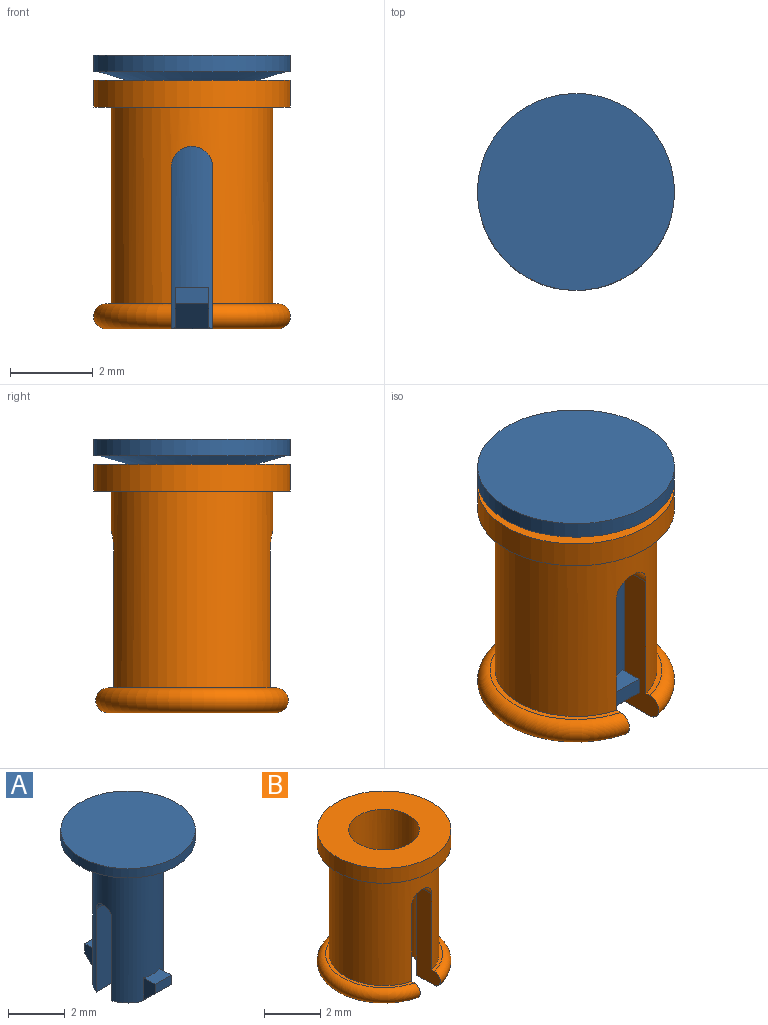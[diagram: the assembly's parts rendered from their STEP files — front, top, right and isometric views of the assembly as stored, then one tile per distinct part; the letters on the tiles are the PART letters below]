
ASSEMBLY  parts=2 mates=1
PART A: 21 faces, bbox 4.8x4.8x6.6 mm
  f0: plane 2.39x0.78mm, normal (0,0,-1), area 1.5mm2, adj f1,f16,f17
  f1: cylinder r=1.25mm len=5.9mm, axis (0,0,1), area 38.8mm2, adj f0,f2,f6,f8,f9,f10,f11,f12
  f2: plane 2.39x0.78mm, normal (0,0,-1), area 1.5mm2, adj f1,f15,f18
  f3: cylinder r=2.38mm len=4.75mm, axis (0,0,1), area 6mm2, adj f4,f5
  f4: plane 4.75x4.75mm, normal (0,0,-1), area 1.8mm2, adj f3,f6
  f5: plane 4.75x4.75mm, normal (0,0,1), area 17.7mm2, adj f3
  f6: cone r=2.25mm half-angle=73.3deg, axis (0,0,1), area 11.5mm2, adj f1,f4
  f7: plane 0.8x0.4mm, normal (0,1,0), area 0.3mm2, adj f8,f9,f10,f16
  f8: plane 0.8x0.57mm, normal (0,0,1), area 0.4mm2, adj f1,f7,f9,f10
  f9: plane 0.97x0.57mm, normal (-1,0,0), area 0.4mm2, adj f1,f7,f8,f16
  f10: plane 0.97x0.57mm, normal (1,0,0), area 0.4mm2, adj f1,f7,f8,f16
  f11: plane 0.8x0.57mm, normal (0,0,1), area 0.4mm2, adj f1,f12,f13,f14
  f12: plane 0.97x0.57mm, normal (1,0,0), area 0.4mm2, adj f1,f11,f14,f15
  f13: plane 0.97x0.57mm, normal (-1,0,0), area 0.4mm2, adj f1,f11,f14,f15
  f14: plane 0.8x0.4mm, normal (0,-1,0), area 0.3mm2, adj f11,f12,f13,f15
  f15: plane 0.98x0.6mm, normal (0,-0.71,-0.71), area 0.7mm2, adj f1,f2,f12,f13,f14
  f16: plane 0.98x0.6mm, normal (0,0.71,-0.71), area 0.7mm2, adj f0,f1,f7,f9,f10
  f17: plane 3.6x2.39mm, normal (0,-1,0), area 8.6mm2, adj f0,f1,f19
  f18: plane 3.6x2.39mm, normal (0,1,0), area 8.6mm2, adj f1,f2,f20
  f19: cylinder r=0.4mm len=2.5mm, axis (1,0,0), area 1.5mm2, adj f1,f17,f20
  f20: cylinder r=0.4mm len=2.5mm, axis (-1,0,0), area 1.5mm2, adj f1,f18,f19
PART B: 17 faces, bbox 5.1x5x6 mm
  f0: plane 4.03x1.58mm, normal (0,0,-1), area 3.5mm2, adj f4,f10,f11,f15
  f1: plane 4.03x1.58mm, normal (0,0,1), area 0.7mm2, adj f2,f3,f12,f16
  f2: torus R=2.08mm, axis (0,0,-1), area 5.8mm2, adj f1,f5,f12,f16
  f3: cylinder r=1.95mm len=4.75mm, axis (0,0,1), area 50.7mm2, adj f1,f8,f9,f11,f12,f13,f14,f15
  f4: cylinder r=1.25mm len=6mm, axis (0,0,1), area 38.3mm2, adj f0,f5,f6,f11,f12,f13,f14,f15
  f5: plane 4.03x1.58mm, normal (0,0,-1), area 3.5mm2, adj f2,f4,f12,f16
  f6: plane 4.75x4.75mm, normal (0,0,1), area 12.8mm2, adj f4,f7
  f7: cylinder r=2.38mm len=4.75mm, axis (0,0,1), area 9.7mm2, adj f6,f8
  f8: plane 4.75x4.75mm, normal (0,0,-1), area 5.8mm2, adj f3,f7
  f9: plane 4.03x1.58mm, normal (0,0,1), area 0.7mm2, adj f3,f10,f11,f15
  f10: torus R=2.08mm, axis (0,0,-1), area 5.8mm2, adj f0,f9,f11,f15
  f11: plane 3.9x1.18mm, normal (-1,0,0), area 3.1mm2, adj f0,f3,f4,f9,f10,f13
  f12: plane 3.9x1.18mm, normal (1,0,0), area 3.1mm2, adj f1,f2,f3,f4,f5,f13
  f13: cylinder r=0.5mm len=1mm, axis (0,-1,0), area 1.1mm2, adj f3,f4,f11,f12
  f14: cylinder r=0.5mm len=1mm, axis (0,-1,0), area 1.1mm2, adj f3,f4,f15,f16
  f15: plane 3.9x1.18mm, normal (-1,0,0), area 3.1mm2, adj f0,f3,f4,f9,f10,f14
  f16: plane 3.9x1.18mm, normal (1,0,0), area 3.1mm2, adj f1,f2,f3,f4,f5,f14
PLACE A at identity
PLACE B at identity
MATE fastened B.f2 <-> A.f1  axis (0,0,-1) through (0,0,-6)mm
